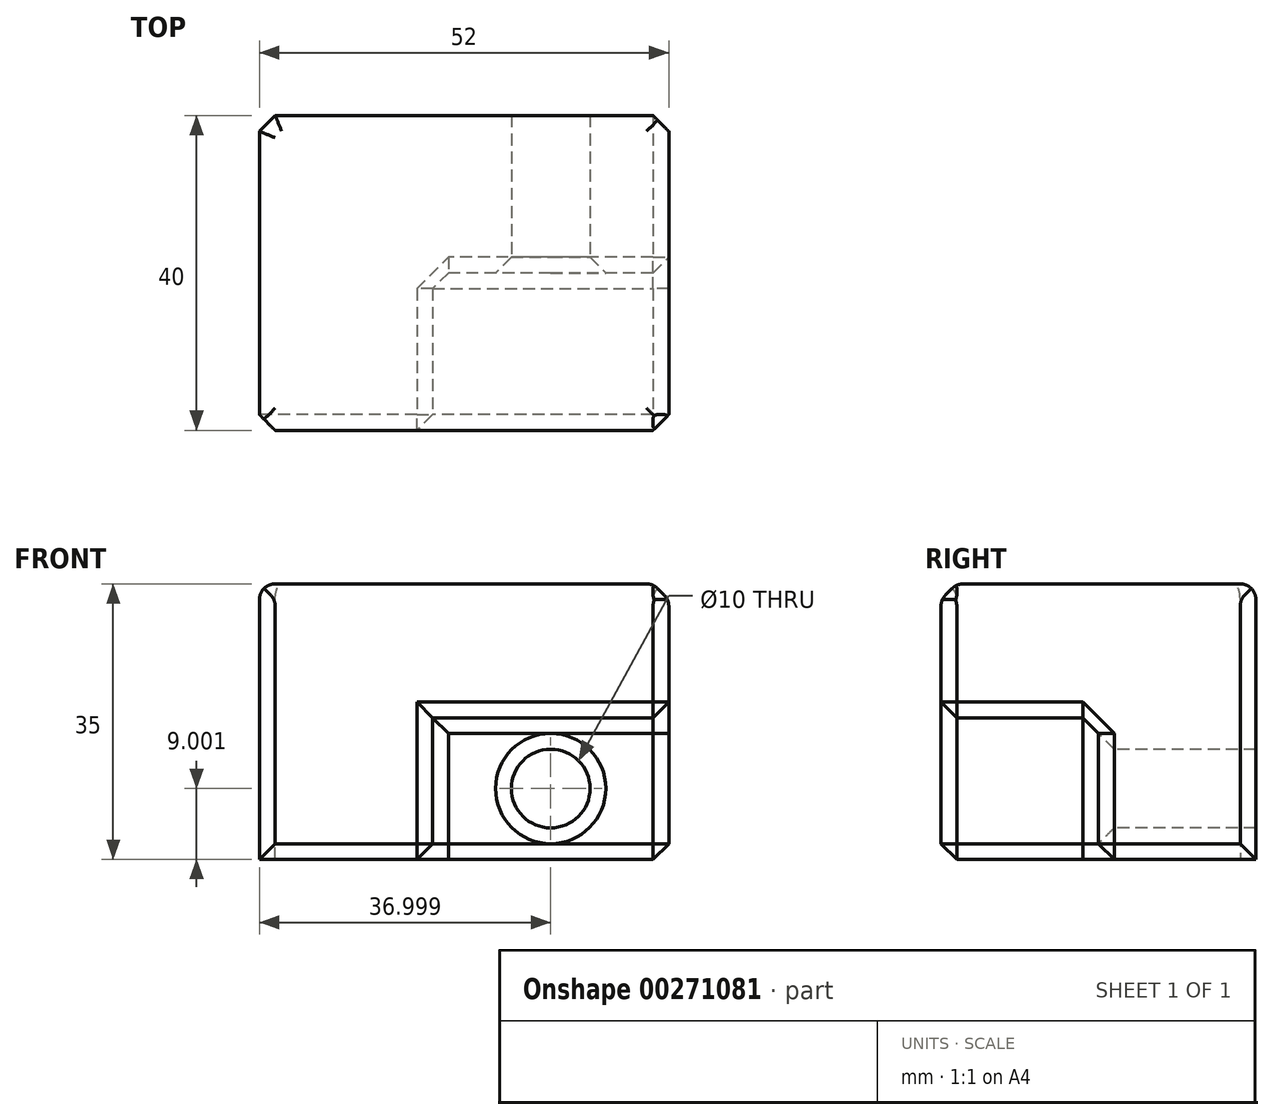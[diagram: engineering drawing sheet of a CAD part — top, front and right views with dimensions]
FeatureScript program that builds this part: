
annotation { "Feature Type Name" : "Feature", "Feature Type Description" : "" }
export const myFeature = defineFeature(function(context is Context, id is Id, definition is map)
    precondition{}
    {
        {
            var Q0;
            Q0=qCreatedBy(makeId("Front.planeOp"),FACE);
            var sketch = newSketch(context, id + "F0", { "sketchPlane" : qUnion([Q0])});
            skLineSegment(sketch, "E0.bottom", {"start": v(-9.17, -10.04) * mm, "end": v(42.83, -10.04) * mm});
            skLineSegment(sketch, "E0.top", {"start": v(-9.17, -45.04) * mm, "end": v(42.83, -45.04) * mm});
            skLineSegment(sketch, "E0.left", {"start": v(-9.17, -10.04) * mm, "end": v(-9.17, -45.04) * mm});
            skLineSegment(sketch, "E0.right", {"start": v(42.83, -10.04) * mm, "end": v(42.83, -45.04) * mm});
            skSolve(sketch);
        }
        {
            var Q0;
            Q0 = qSketchRegion(id + "F0", true);
            extrude(context, id + "F1", {"entities" : qUnion([Q0]), "depth" : 40 * mm});
        }
        {
            var Q0;
            Q0=makeQuery(id+"F1.opExtrude","CAP_FACE",FACE,{"disambiguationData":[OSD([sQuery(id+"F0.wireOp",EDGE,"E0.bottom"),sQuery(id+"F0.wireOp",EDGE,"E0.top"),sQuery(id+"F0.wireOp",EDGE,"E0.left"),sQuery(id+"F0.wireOp",EDGE,"E0.right")])],"isStart":false});
            var sketch = newSketch(context, id + "F2", { "sketchPlane" : qUnion([Q0])});
            skLineSegment(sketch, "E1.bottom", {"start": v(42.83, -45.04) * mm, "end": v(12.83, -45.04) * mm});
            skLineSegment(sketch, "E1.top", {"start": v(42.83, -27.04) * mm, "end": v(12.83, -27.04) * mm});
            skLineSegment(sketch, "E1.left", {"start": v(42.83, -45.04) * mm, "end": v(42.83, -27.04) * mm});
            skLineSegment(sketch, "E1.right", {"start": v(12.83, -45.04) * mm, "end": v(12.83, -27.04) * mm});
            skSolve(sketch);
        }
        {
            var Q0;
            Q0 = qSketchRegion(id + "F2", true);
            extrude(context, id + "F3", {"entities" : qUnion([Q0]), "operationType" : NewBodyOperationType.REMOVE, "oppositeDirection" : true, "depth" : 20 * mm});
        }
        {
            var Q0;
            Q0=makeQuery(id+"F3.boolean.opBoolean","COPY",FACE,{"derivedFrom":makeQuery(id+"F3.opExtrude","CAP_FACE",FACE,{"disambiguationData":[OSD([sQuery(id+"F2.wireOp",EDGE,"E1.bottom"),sQuery(id+"F2.wireOp",EDGE,"E1.top"),sQuery(id+"F2.wireOp",EDGE,"E1.left"),sQuery(id+"F2.wireOp",EDGE,"E1.right")])],"isStart":false})});
            var sketch = newSketch(context, id + "F4", { "sketchPlane" : qUnion([Q0])});
            skCircle(sketch, "E2", {"center": v(27.83, -36.04) * mm, "radius": 5 * mm});
            skPoint(sketch, "E2.centerSnap0", {"position": v(27.83, -45.04) * mm});
            skPoint(sketch, "E2.centerSnap1", {"position": v(42.83, -36.04) * mm});
            skSolve(sketch);
        }
        {
            var Q0;
            Q0 = qSketchRegion(id + "F4", true);
            extrude(context, id + "F5", {"entities" : qUnion([Q0]), "operationType" : NewBodyOperationType.REMOVE, "endBound" : BoundingType.THROUGH_ALL, "oppositeDirection" : true, "depth" : 25 * mm});
        }
        {
            var Q0;
            Q0=makeQuery(id+"F1.opExtrude","CAP_FACE",FACE,{"disambiguationData":[OSD([sQuery(id+"F0.wireOp",EDGE,"E0.bottom"),sQuery(id+"F0.wireOp",EDGE,"E0.top"),sQuery(id+"F0.wireOp",EDGE,"E0.left"),sQuery(id+"F0.wireOp",EDGE,"E0.right")])],"isStart":false});
            var Q1;
            Q1=makeQuery(id+"F1.opExtrude","CAP_EDGE",EDGE,{"disambiguationData":[OSD([sQuery(id+"F0.wireOp",EDGE,"E0.left")])],"isStart":true});
            var Q2;
            Q2=makeQuery(id+"F3.boolean.opBoolean","COPY",FACE,{"derivedFrom":makeQuery(id+"F3.opExtrude","CAP_FACE",FACE,{"disambiguationData":[OSD([sQuery(id+"F2.wireOp",EDGE,"E1.bottom"),sQuery(id+"F2.wireOp",EDGE,"E1.top"),sQuery(id+"F2.wireOp",EDGE,"E1.left"),sQuery(id+"F2.wireOp",EDGE,"E1.right")])],"isStart":false})});
            var Q3;
            Q3=makeQuery(id+"F1.opExtrude","SWEPT_FACE",FACE,{"disambiguationData":[OSD([sQuery(id+"F0.wireOp",EDGE,"E0.right")])]});
            chamfer(context, id + "F6", {"entities" : qUnion([Q0, Q1, Q2, Q3]), "width" : 2 * mm, "tangentPropagation" : true});
        }
        {
            var Q0;
            {var subQ0=sQuery(id+"F0.wireOp",EDGE,"E0.bottom");Q0=makeQuery(id+"F6.opChamfer","BLEND_EDGE",EDGE,{"blendedFrom":[makeQuery(id+"F1.opExtrude","CAP_EDGE",EDGE,{"disambiguationData":[OSD([subQ0])],"isStart":true}),makeQuery(id+"F1.opExtrude","SWEPT_FACE",FACE,{"disambiguationData":[OSD([subQ0])]})],"blendedInto":[makeQuery(id+"F1.opExtrude","SWEPT_FACE",FACE,{"disambiguationData":[OSD([subQ0])]})]});}
            var Q1;
            {var subQ0=sQuery(id+"F0.wireOp",EDGE,"E0.bottom");Q1=makeQuery(id+"F6.opChamfer","BLEND_EDGE",EDGE,{"blendedFrom":[makeQuery(id+"F1.opExtrude","CAP_EDGE",EDGE,{"disambiguationData":[OSD([subQ0])],"isStart":true}),makeQuery(id+"F1.opExtrude","CAP_FACE",FACE,{"disambiguationData":[OSD([subQ0,sQuery(id+"F0.wireOp",EDGE,"E0.top"),sQuery(id+"F0.wireOp",EDGE,"E0.left"),sQuery(id+"F0.wireOp",EDGE,"E0.right")])],"isStart":true})],"blendedInto":[makeQuery(id+"F1.opExtrude","CAP_FACE",FACE,{"disambiguationData":[OSD([subQ0,sQuery(id+"F0.wireOp",EDGE,"E0.top"),sQuery(id+"F0.wireOp",EDGE,"E0.left"),sQuery(id+"F0.wireOp",EDGE,"E0.right")])],"isStart":true})]});}
            var Q2;
            {var subQ0=sQuery(id+"F0.wireOp",EDGE,"E0.bottom");Q2=makeQuery(id+"F6.opChamfer","BLEND_EDGE",EDGE,{"blendedFrom":[makeQuery(id+"F1.opExtrude","SWEPT_EDGE",EDGE,{"disambiguationData":[OSD([subQ0,sQuery(id+"F0.wireOp",EDGE,"E0.left")])]}),makeQuery(id+"F1.opExtrude","SWEPT_FACE",FACE,{"disambiguationData":[OSD([subQ0])]})],"blendedInto":[makeQuery(id+"F1.opExtrude","SWEPT_FACE",FACE,{"disambiguationData":[OSD([subQ0])]})]});}
            var Q3;
            {var subQ0=sQuery(id+"F0.wireOp",EDGE,"E0.left");Q3=makeQuery(id+"F6.opChamfer","BLEND_EDGE",EDGE,{"blendedFrom":[makeQuery(id+"F1.opExtrude","SWEPT_EDGE",EDGE,{"disambiguationData":[OSD([sQuery(id+"F0.wireOp",EDGE,"E0.bottom"),subQ0])]}),makeQuery(id+"F1.opExtrude","SWEPT_FACE",FACE,{"disambiguationData":[OSD([subQ0])]})],"blendedInto":[makeQuery(id+"F1.opExtrude","SWEPT_FACE",FACE,{"disambiguationData":[OSD([subQ0])]})]});}
            var Q4;
            {var subQ0=sQuery(id+"F0.wireOp",EDGE,"E0.right");var subQ1=sQuery(id+"F0.wireOp",EDGE,"E0.bottom");Q4=makeQuery(id+"F6.opChamfer","BLEND_EDGE",EDGE,{"blendedFrom":[makeQuery(id+"F1.opExtrude","CAP_VERTEX",VERTEX,{"disambiguationData":[OSD([subQ1,subQ0])],"isStart":true}),makeQuery(id+"F1.opExtrude","SWEPT_EDGE",EDGE,{"disambiguationData":[OSD([subQ1,subQ0])]})],"blendedInto":[]});}
            var Q5;
            {var subQ0=sQuery(id+"F0.wireOp",EDGE,"E0.right");Q5=makeQuery(id+"F6.opChamfer","BLEND_EDGE",EDGE,{"blendedFrom":[makeQuery(id+"F1.opExtrude","SWEPT_EDGE",EDGE,{"disambiguationData":[OSD([sQuery(id+"F0.wireOp",EDGE,"E0.bottom"),subQ0])]}),makeQuery(id+"F1.opExtrude","SWEPT_FACE",FACE,{"disambiguationData":[OSD([subQ0])]})],"blendedInto":[makeQuery(id+"F1.opExtrude","SWEPT_FACE",FACE,{"disambiguationData":[OSD([subQ0])]})]});}
            var Q6;
            {var subQ0=sQuery(id+"F0.wireOp",EDGE,"E0.bottom");Q6=makeQuery(id+"F6.opChamfer","BLEND_EDGE",EDGE,{"blendedFrom":[makeQuery(id+"F1.opExtrude","SWEPT_EDGE",EDGE,{"disambiguationData":[OSD([subQ0,sQuery(id+"F0.wireOp",EDGE,"E0.right")])]}),makeQuery(id+"F1.opExtrude","SWEPT_FACE",FACE,{"disambiguationData":[OSD([subQ0])]})],"blendedInto":[makeQuery(id+"F1.opExtrude","SWEPT_FACE",FACE,{"disambiguationData":[OSD([subQ0])]})]});}
            var Q7;
            Q7=makeQuery(id+"F1.opExtrude","SWEPT_FACE",FACE,{"disambiguationData":[OSD([sQuery(id+"F0.wireOp",EDGE,"E0.bottom")])]});
            var Q8;
            {var subQ0=sQuery(id+"F0.wireOp",EDGE,"E0.bottom");Q8=makeQuery(id+"F6.opChamfer","BLEND_EDGE",EDGE,{"blendedFrom":[makeQuery(id+"F1.opExtrude","CAP_EDGE",EDGE,{"disambiguationData":[OSD([subQ0])],"isStart":false}),makeQuery(id+"F1.opExtrude","CAP_FACE",FACE,{"disambiguationData":[OSD([subQ0,sQuery(id+"F0.wireOp",EDGE,"E0.top"),sQuery(id+"F0.wireOp",EDGE,"E0.left"),sQuery(id+"F0.wireOp",EDGE,"E0.right")])],"isStart":false})],"blendedInto":[makeQuery(id+"F1.opExtrude","CAP_FACE",FACE,{"disambiguationData":[OSD([subQ0,sQuery(id+"F0.wireOp",EDGE,"E0.top"),sQuery(id+"F0.wireOp",EDGE,"E0.left"),sQuery(id+"F0.wireOp",EDGE,"E0.right")])],"isStart":false})]});}
            fillet(context, id + "F7", {"entities" : qUnion([Q0, Q1, Q2, Q3, Q4, Q5, Q6, Q7, Q8]), "radius" : 2 * mm, "tangentPropagation" : true, "allowEdgeOverflow" : false});
        }
    });
